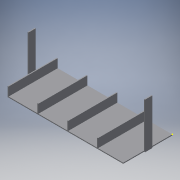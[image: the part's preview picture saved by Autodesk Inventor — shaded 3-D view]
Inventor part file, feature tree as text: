
AUTODESK INVENTOR PART (.ipt)
format: ipt  version: 2016 (Build 200138000, 138)  size: 158,208 bytes
history: native  units: in
note: dims shown in document units (in); Inventor stores cm internally (conversion verified against a paired STEP export)
features: sketch x8, extrude x7
ambient origin geometry x8: Origin, YZ Plane, XZ Plane, XY Plane, X Axis, Y Axis, Z Axis, Center Point
bodies: Solid1 (feature_tree)
feature tree (15):
  extrude  "Extrusion1"  Depth=0.063in
  extrude  "Extrusion2"  Depth=0.063in
  extrude  "Extrusion3"  Depth=0.063in
  extrude  "Extrusion4"  Depth=0.063in
  extrude  "Extrusion5"  Depth=0.063in
  extrude  "Extrusion6"  Depth=0.5in
  extrude  "Extrusion7"  Depth=0.063in TaperAngle=0.0deg
  sketch  "Sketch8"  dims[d20=3.15in d21=0.063in d22=0.0in]
  sketch  "Sketch1"  dims[d0=8.0in d1=0.063in]
  sketch  "Sketch2"  dims[d2=3.4in d3=0.0in d4=0.063in]
  sketch  "Sketch3"  dims[d5=0.6in d6=0.0in d7=0.063in]
  sketch  "Sketch4"  dims[d8=0.6in d9=0.0in d10=0.063in]
  sketch  "Sketch5"  dims[d11=0.6in d12=0.0in d13=0.063in]
  sketch  "Sketch6"  dims[d14=0.6in d15=0.0in d16=0.5in]
  sketch  "Sketch7"  dims[d17=3.15in d18=0.063in d19=0.0in]
